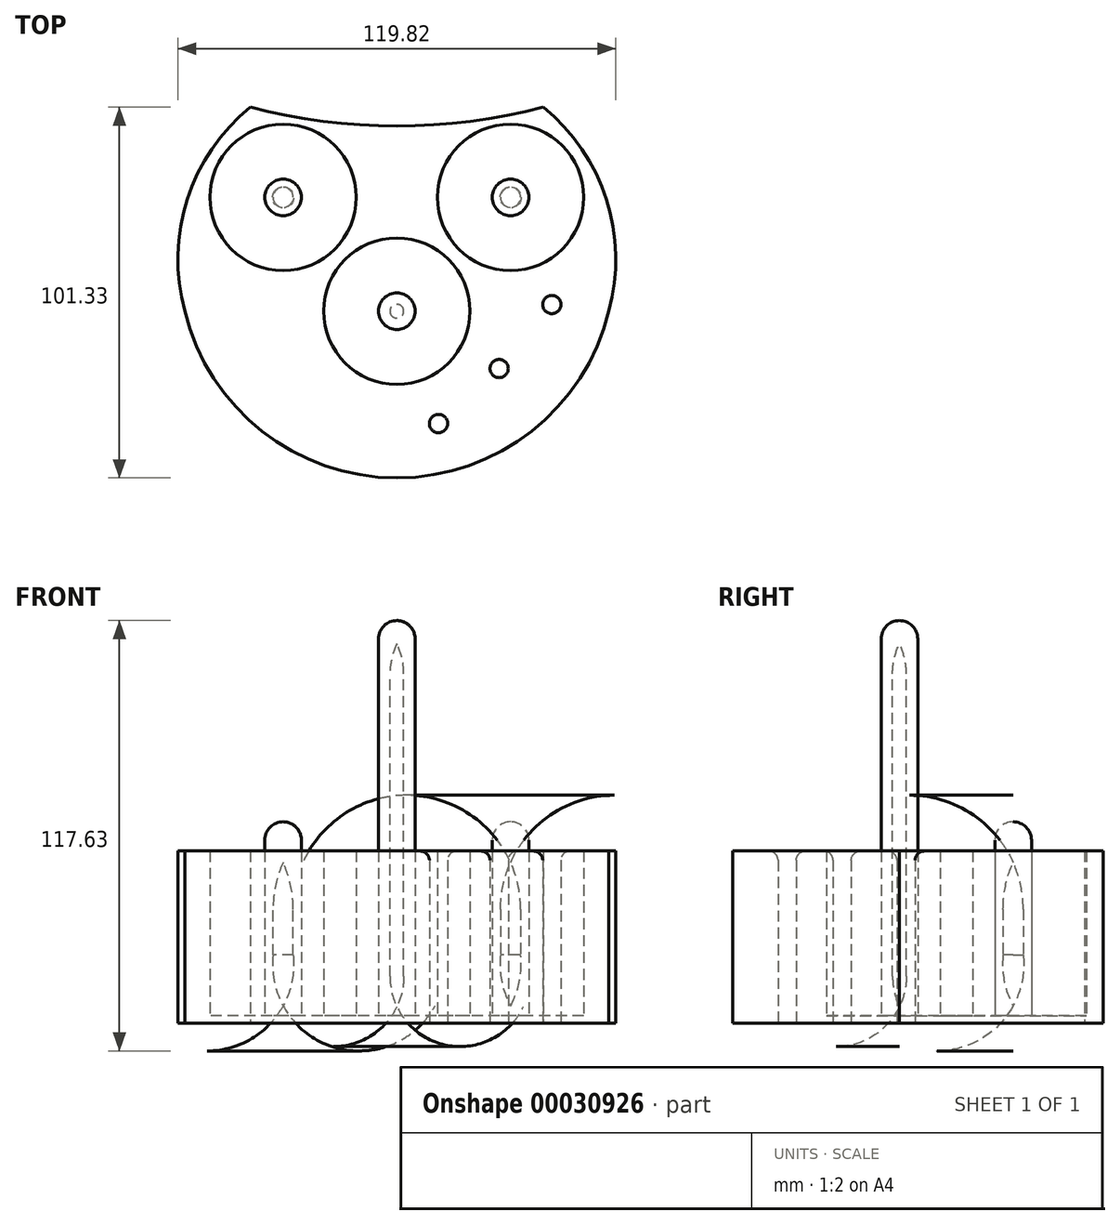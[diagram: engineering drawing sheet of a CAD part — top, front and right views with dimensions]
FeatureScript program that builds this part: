
annotation { "Feature Type Name" : "Feature", "Feature Type Description" : "" }
export const myFeature = defineFeature(function(context is Context, id is Id, definition is map)
    precondition{}
    {
        {
            var Q0;
            Q0=qCreatedBy(makeId("Top.planeOp"),FACE);
            var sketch = newSketch(context, id + "F0", { "sketchPlane" : qUnion([Q0])});
            skCircle(sketch, "E0", {"center": v(31.11, 31.11) * mm, "radius": 20 * mm});
            skCircle(sketch, "E1", {"center": v(0, 0) * mm, "radius": 20 * mm});
            skCircle(sketch, "E2", {"center": v(-31.11, 31.11) * mm, "radius": 20 * mm});
            skCircle(sketch, "E3", {"center": v(-0.1, 36.45) * mm, "radius": 10.5 * mm, "construction": true});
            skCircle(sketch, "E4", {"center": v(-42.4, 1.8) * mm, "radius": 10.5 * mm, "construction": true});
            skLineSegment(sketch, "E5", {"start": v(0, 0) * mm, "end": v(-31.11, 31.11) * mm, "construction": true});
            skLineSegment(sketch, "E6", {"start": v(0, 0) * mm, "end": v(31.11, 31.11) * mm, "construction": true});
            skLineSegment(sketch, "E7", {"start": v(0, 0) * mm, "end": v(0, 31.6) * mm, "construction": true});
            skCircle(sketch, "E8", {"center": v(-27.98, -15.68) * mm, "radius": 10.5 * mm, "construction": true});
            skCircle(sketch, "E9", {"center": v(-11.4, -30.72) * mm, "radius": 10.5 * mm, "construction": true});
            skLineSegment(sketch, "E10", {"start": v(0, 0) * mm, "end": v(0, -39.18) * mm, "construction": true});
            skCircle(sketch, "E11", {"center": v(-42.4, 1.8) * mm, "radius": 2.5 * mm});
            skCircle(sketch, "E12", {"center": v(-27.98, -15.68) * mm, "radius": 2.5 * mm});
            skCircle(sketch, "E13", {"center": v(-11.4, -30.72) * mm, "radius": 2.5 * mm});
            skCircle(sketch, "E14.MirrorC", {"center": v(11.4, -30.72) * mm, "radius": 2.5 * mm});
            skCircle(sketch, "E15.MirrorC", {"center": v(42.4, 1.8) * mm, "radius": 2.5 * mm});
            skCircle(sketch, "E16.MirrorC", {"center": v(42.4, 1.8) * mm, "radius": 10.5 * mm, "construction": true});
            skCircle(sketch, "E17.MirrorC", {"center": v(27.98, -15.68) * mm, "radius": 10.5 * mm, "construction": true});
            skCircle(sketch, "E18.MirrorC", {"center": v(27.98, -15.68) * mm, "radius": 2.5 * mm});
            skCircle(sketch, "E19.MirrorC", {"center": v(11.4, -30.72) * mm, "radius": 10.5 * mm, "construction": true});
            skArc(sketch, "E20", {"start": v(-58, 0) * mm, "mid": v(0, -45.58) * mm, "end": v(58, 0) * mm});
            skArc(sketch, "E21", {"start": v(-40.1, 55.75) * mm, "mid": v(-57.35, 30.54) * mm, "end": v(-58, 0) * mm});
            skArc(sketch, "E22.MirrorCS", {"start": v(40.1, 55.75) * mm, "mid": v(57.35, 30.54) * mm, "end": v(58, 0) * mm});
            skArc(sketch, "E23", {"start": v(-40.1, 55.75) * mm, "mid": v(0, 50.6) * mm, "end": v(40.1, 55.75) * mm});
            skCircle(sketch, "E24", {"center": v(-31.11, 31.11) * mm, "radius": 5 * mm});
            skCircle(sketch, "E25", {"center": v(31.11, 31.11) * mm, "radius": 5 * mm});
            skCircle(sketch, "E26", {"center": v(0, 0) * mm, "radius": 5 * mm});
            skCircle(sketch, "E27", {"center": v(-0.1, 36.45) * mm, "radius": 2.5 * mm});
            skSolve(sketch);
        }
        {
            var Q0;
            Q0=makeQuery(id+"F0.imprint","IMPRINT",FACE,{"disambiguationData":[TD([[makeQuery(id+"F0.imprint","IMPRINT",EDGE,{"derivedFrom":sQuery(id+"F0.wireOp",EDGE,"E0")}),-1.0]])]});
            var Q1;
            Q1=makeQuery(id+"F0.imprint","IMPRINT",FACE,{"disambiguationData":[TD([[makeQuery(id+"F0.imprint","IMPRINT",EDGE,{"derivedFrom":sQuery(id+"F0.wireOp",EDGE,"E1")}),1.0]])]});
            var Q2;
            Q2=makeQuery(id+"F0.imprint","IMPRINT",FACE,{"disambiguationData":[TD([[makeQuery(id+"F0.imprint","IMPRINT",EDGE,{"derivedFrom":sQuery(id+"F0.wireOp",EDGE,"E2")}),1.0]])]});
            var Q3;
            Q3=makeQuery(id+"F0.imprint","IMPRINT",FACE,{"disambiguationData":[TD([[makeQuery(id+"F0.imprint","IMPRINT",EDGE,{"derivedFrom":sQuery(id+"F0.wireOp",EDGE,"E0")}),1.0]])]});
            extrude(context, id + "F1", {"entities" : qUnion([Q0, Q1, Q2, Q3]), "depth" : 2 * mm});
        }
        {
            var Q0;
            Q0=makeQuery(id+"F0.imprint","IMPRINT",FACE,{"disambiguationData":[TD([[makeQuery(id+"F0.imprint","IMPRINT",EDGE,{"derivedFrom":sQuery(id+"F0.wireOp",EDGE,"E14.MirrorC")}),-1.0]])]});
            var Q1;
            Q1=makeQuery(id+"F0.imprint","IMPRINT",FACE,{"disambiguationData":[TD([[makeQuery(id+"F0.imprint","IMPRINT",EDGE,{"derivedFrom":sQuery(id+"F0.wireOp",EDGE,"E13")}),1.0]])]});
            var Q2;
            Q2=makeQuery(id+"F0.imprint","IMPRINT",FACE,{"disambiguationData":[TD([[makeQuery(id+"F0.imprint","IMPRINT",EDGE,{"derivedFrom":sQuery(id+"F0.wireOp",EDGE,"E12")}),1.0]])]});
            var Q3;
            Q3=makeQuery(id+"F0.imprint","IMPRINT",FACE,{"disambiguationData":[TD([[makeQuery(id+"F0.imprint","IMPRINT",EDGE,{"derivedFrom":sQuery(id+"F0.wireOp",EDGE,"E11")}),1.0]])]});
            var Q4;
            Q4=makeQuery(id+"F0.imprint","IMPRINT",FACE,{"disambiguationData":[TD([[makeQuery(id+"F0.imprint","IMPRINT",EDGE,{"derivedFrom":sQuery(id+"F0.wireOp",EDGE,"E18.MirrorC")}),-1.0]])]});
            var Q5;
            Q5=makeQuery(id+"F0.imprint","IMPRINT",FACE,{"disambiguationData":[TD([[makeQuery(id+"F0.imprint","IMPRINT",EDGE,{"derivedFrom":sQuery(id+"F0.wireOp",EDGE,"E15.MirrorC")}),-1.0]])]});
            var Q6;
            Q6=makeQuery(id+"F0.imprint","IMPRINT",FACE,{"disambiguationData":[TD([[makeQuery(id+"F0.imprint","IMPRINT",EDGE,{"derivedFrom":sQuery(id+"F0.wireOp",EDGE,"E27")}),1.0]])]});
            extrude(context, id + "F2", {"entities" : qUnion([Q0, Q1, Q2, Q3, Q4, Q5, Q6]), "operationType" : NewBodyOperationType.ADD, "depth" : 47 * mm});
        }
        {
            var Q0;
            Q0=makeQuery(id+"F0.imprint","IMPRINT",FACE,{"disambiguationData":[TD([[makeQuery(id+"F0.imprint","IMPRINT",EDGE,{"derivedFrom":sQuery(id+"F0.wireOp",EDGE,"E26")}),1.0]])]});
            extrude(context, id + "F3", {"entities" : qUnion([Q0]), "operationType" : NewBodyOperationType.ADD, "depth" : 110 * mm});
        }
        {
            var Q0;
            Q0=makeQuery(id+"F0.imprint","IMPRINT",FACE,{"disambiguationData":[TD([[makeQuery(id+"F0.imprint","IMPRINT",EDGE,{"derivedFrom":sQuery(id+"F0.wireOp",EDGE,"E25")}),1.0]])]});
            var Q1;
            Q1=makeQuery(id+"F0.imprint","IMPRINT",FACE,{"disambiguationData":[TD([[makeQuery(id+"F0.imprint","IMPRINT",EDGE,{"derivedFrom":sQuery(id+"F0.wireOp",EDGE,"E24")}),1.0]])]});
            extrude(context, id + "F4", {"entities" : qUnion([Q0, Q1]), "operationType" : NewBodyOperationType.ADD, "depth" : 55 * mm});
        }
        {
            var Q0;
            Q0=makeQuery(id+"F2.opExtrude","CAP_EDGE",EDGE,{"disambiguationData":[OSD([sQuery(id+"F0.wireOp",EDGE,"E12")])],"isStart":false});
            var Q1;
            Q1=makeQuery(id+"F2.opExtrude","CAP_EDGE",EDGE,{"disambiguationData":[OSD([sQuery(id+"F0.wireOp",EDGE,"E11")])],"isStart":false});
            var Q2;
            Q2=makeQuery(id+"F2.opExtrude","CAP_EDGE",EDGE,{"disambiguationData":[OSD([sQuery(id+"F0.wireOp",EDGE,"E13")])],"isStart":false});
            var Q3;
            Q3=makeQuery(id+"F2.opExtrude","CAP_EDGE",EDGE,{"disambiguationData":[OSD([sQuery(id+"F0.wireOp",EDGE,"E14.MirrorC")])],"isStart":false});
            var Q4;
            Q4=makeQuery(id+"F2.opExtrude","CAP_EDGE",EDGE,{"disambiguationData":[OSD([sQuery(id+"F0.wireOp",EDGE,"E18.MirrorC")])],"isStart":false});
            var Q5;
            Q5=makeQuery(id+"F2.opExtrude","CAP_EDGE",EDGE,{"disambiguationData":[OSD([sQuery(id+"F0.wireOp",EDGE,"E15.MirrorC")])],"isStart":false});
            var Q6;
            Q6=makeQuery(id+"F2.opExtrude","CAP_FACE",FACE,{"disambiguationData":[OSD([sQuery(id+"F0.wireOp",EDGE,"E27")])],"isStart":false});
            fillet(context, id + "F5", {"entities" : qUnion([Q0, Q1, Q2, Q3, Q4, Q5, Q6]), "radius" : 2.5 * mm, "tangentPropagation" : true, "allowEdgeOverflow" : false});
        }
        {
            var Q0;
            Q0=makeQuery(id+"F4.opExtrude","CAP_EDGE",EDGE,{"disambiguationData":[OSD([sQuery(id+"F0.wireOp",EDGE,"E26")])],"isStart":false});
            var Q1;
            Q1=makeQuery(id+"F4.opExtrude","CAP_EDGE",EDGE,{"disambiguationData":[OSD([sQuery(id+"F0.wireOp",EDGE,"E25")])],"isStart":false});
            var Q2;
            Q2=makeQuery(id+"F4.opExtrude","CAP_EDGE",EDGE,{"disambiguationData":[OSD([sQuery(id+"F0.wireOp",EDGE,"E24")])],"isStart":false});
            var Q3;
            Q3=makeQuery(id+"F3.opExtrude","CAP_FACE",FACE,{"disambiguationData":[OSD([sQuery(id+"F0.wireOp",EDGE,"E26")])],"isStart":false});
            fillet(context, id + "F6", {"entities" : qUnion([Q0, Q1, Q2, Q3]), "radius" : 5 * mm, "tangentPropagation" : true, "allowEdgeOverflow" : false});
        }
        {
            var Q0;
            Q0=qCreatedBy(makeId("Front.planeOp"),FACE);
            var sketch = newSketch(context, id + "F7", { "sketchPlane" : qUnion([Q0])});
            skLineSegment(sketch, "E28", {"start": v(-1.89, 12.75) * mm, "end": v(-1.89, 95.45) * mm});
            skArc(sketch, "E29", {"start": v(0, 103.64) * mm, "mid": v(-1.4, 99.65) * mm, "end": v(-1.89, 95.45) * mm});
            skArc(sketch, "E30", {"start": v(-1.89, 12.75) * mm, "mid": v(-1.4, 8.5) * mm, "end": v(0, 4.45) * mm});
            skLineSegment(sketch, "E31", {"start": v(0, 4.45) * mm, "end": v(0, 103.64) * mm});
            skSolve(sketch);
        }
        {
            var Q0;
            Q0 = qSketchRegion(id + "F7", true);
            var Q1;
            Q1=sQuery(id+"F7.wireOp",EDGE,"E31");
            revolve(context, id + "F8", {"operationType" : NewBodyOperationType.REMOVE, "entities" : qUnion([Q0]), "axis" : qUnion([Q1]), "revolveType" : RevolveType.FULL, "oppositeDirection" : true});
        }
        {
            var Q0;
            Q0=qCreatedBy(makeId("Front.planeOp"),FACE);
            cPlane(context, id + "F9", {"entities" : qUnion([Q0]), "cplaneType" : CPlaneType.OFFSET, "offset" : 31.11 * mm, "oppositeDirection" : true, "width" : 150 * mm, "height" : 150 * mm});
        }
        {
            var Q0;
            Q0=qCreatedBy(id+"F9.planeOp",FACE);
            var sketch = newSketch(context, id + "F10", { "sketchPlane" : qUnion([Q0])});
            skLineSegment(sketch, "E32.0", {"start": v(26.11, 2) * mm, "end": v(36.11, 2) * mm});
            skLineSegment(sketch, "E33", {"start": v(31.11, 4.7) * mm, "end": v(31.11, 43.9) * mm});
            skPoint(sketch, "E33.startSnap0", {"position": v(31.11, 2) * mm});
            skArc(sketch, "E34", {"start": v(28.36, 18.6) * mm, "mid": v(28.67, 11.44) * mm, "end": v(31.11, 4.7) * mm});
            skLineSegment(sketch, "E35", {"start": v(28.36, 18.6) * mm, "end": v(28.36, 31.1) * mm});
            skArc(sketch, "E36", {"start": v(31.11, 43.9) * mm, "mid": v(29.06, 37.65) * mm, "end": v(28.36, 31.1) * mm});
            skLineSegment(sketch, "E37", {"start": v(0, 0) * mm, "end": v(0, 34.2) * mm, "construction": true});
            skLineSegment(sketch, "E38.MirrorCS", {"start": v(-31.11, 4.7) * mm, "end": v(-31.11, 43.9) * mm});
            skArc(sketch, "E39.MirrorCS", {"start": v(-31.11, 43.9) * mm, "mid": v(-33.17, 37.65) * mm, "end": v(-33.86, 31.1) * mm});
            skLineSegment(sketch, "E40.MirrorCS", {"start": v(-33.86, 18.6) * mm, "end": v(-33.86, 31.1) * mm});
            skArc(sketch, "E41.MirrorCS", {"start": v(-33.86, 18.6) * mm, "mid": v(-33.55, 11.44) * mm, "end": v(-31.11, 4.7) * mm});
            skSolve(sketch);
        }
        {
            var Q0;
            Q0=makeQuery(id+"F10.imprint","IMPRINT",FACE,{"disambiguationData":[TD([[makeQuery(id+"F10.imprint","IMPRINT",EDGE,{"derivedFrom":sQuery(id+"F10.wireOp",EDGE,"E33")}),1.0]])]});
            var Q1;
            Q1=sQuery(id+"F10.wireOp",EDGE,"E33");
            revolve(context, id + "F11", {"operationType" : NewBodyOperationType.REMOVE, "entities" : qUnion([Q0]), "axis" : qUnion([Q1]), "revolveType" : RevolveType.FULL});
        }
        {
            var Q0;
            Q0=makeQuery(id+"F10.imprint","IMPRINT",FACE,{"disambiguationData":[TD([[makeQuery(id+"F10.imprint","IMPRINT",EDGE,{"derivedFrom":sQuery(id+"F10.wireOp",EDGE,"E38.MirrorCS")}),1.0]])]});
            var Q1;
            Q1=sQuery(id+"F10.wireOp",EDGE,"E38.MirrorCS");
            revolve(context, id + "F12", {"operationType" : NewBodyOperationType.REMOVE, "entities" : qUnion([Q0]), "axis" : qUnion([Q1]), "revolveType" : RevolveType.FULL, "oppositeDirection" : true});
        }
    });
